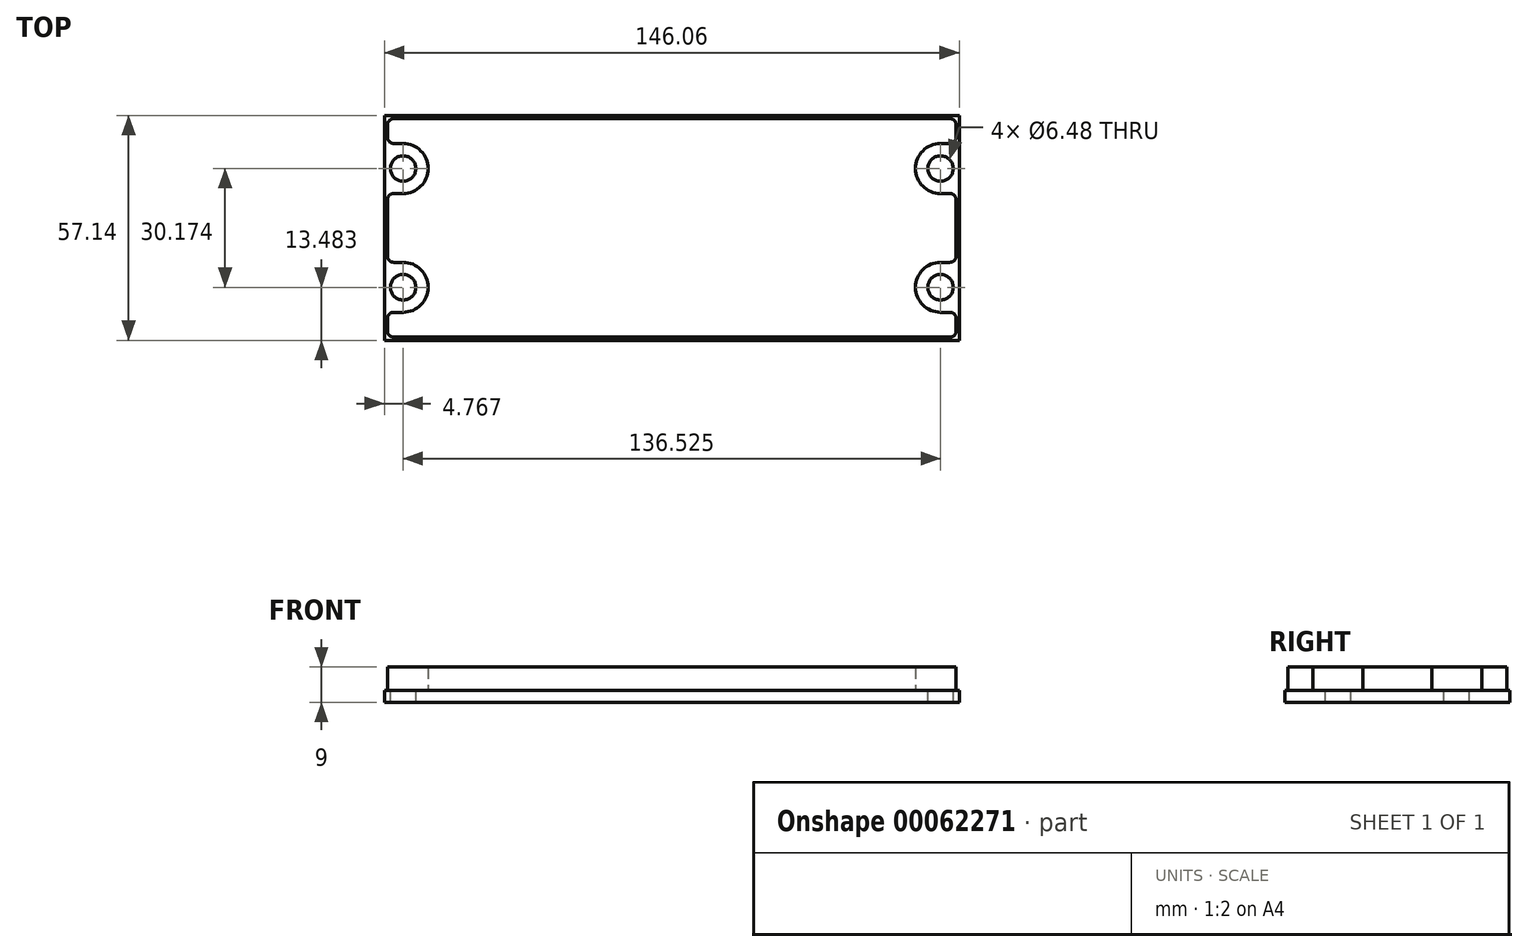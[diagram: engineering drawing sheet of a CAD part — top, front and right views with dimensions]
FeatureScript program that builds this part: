
annotation { "Feature Type Name" : "Feature", "Feature Type Description" : "" }
export const myFeature = defineFeature(function(context is Context, id is Id, definition is map)
    precondition{}
    {
        {
            var Q0;
            Q0=qCreatedBy(makeId("Top.planeOp"),FACE);
            var sketch = newSketch(context, id + "F0", { "sketchPlane" : qUnion([Q0])});
            skLineSegment(sketch, "E0.bottom", {"start": v(73.02, 28.57) * mm, "end": v(-73.03, 28.57) * mm});
            skLineSegment(sketch, "E0.top", {"start": v(73.02, -28.57) * mm, "end": v(-73.03, -28.57) * mm});
            skLineSegment(sketch, "E0.left", {"start": v(73.02, 28.57) * mm, "end": v(73.02, -28.57) * mm});
            skLineSegment(sketch, "E0.right", {"start": v(-73.03, 28.57) * mm, "end": v(-73.03, -28.57) * mm});
            skPoint(sketch, "E0.middle", {"position": v(0, 0) * mm});
            skLineSegment(sketch, "E1.bottom", {"start": v(72.22, 27.78) * mm, "end": v(-72.22, 27.78) * mm});
            skLineSegment(sketch, "E1.top", {"start": v(72.22, -27.78) * mm, "end": v(-72.22, -27.78) * mm});
            skLineSegment(sketch, "E1.left", {"start": v(72.22, 27.78) * mm, "end": v(72.22, 21.44) * mm});
            skLineSegment(sketch, "E1.right", {"start": v(-72.22, 27.78) * mm, "end": v(-72.22, 21.44) * mm});
            skArc(sketch, "E2", {"start": v(-68.26, 8.74) * mm, "mid": v(-61.91, 15.09) * mm, "end": v(-68.26, 21.44) * mm});
            skLineSegment(sketch, "E3", {"start": v(-68.26, 21.44) * mm, "end": v(-72.22, 21.44) * mm});
            skLineSegment(sketch, "E4", {"start": v(-68.26, 8.74) * mm, "end": v(-72.22, 8.74) * mm});
            skLineSegment(sketch, "E5.trimOffspring", {"start": v(-72.22, 8.74) * mm, "end": v(-72.22, -8.74) * mm});
            skCircle(sketch, "E6", {"center": v(-68.26, 15.09) * mm, "radius": 3.24 * mm});
            skLineSegment(sketch, "E7.MirrorCS", {"start": v(-68.26, -21.44) * mm, "end": v(-72.22, -21.44) * mm});
            skArc(sketch, "E8.MirrorCS", {"start": v(-68.26, -8.74) * mm, "mid": v(-61.91, -15.09) * mm, "end": v(-68.26, -21.44) * mm});
            skCircle(sketch, "E9.MirrorC", {"center": v(-68.26, -15.09) * mm, "radius": 3.24 * mm});
            skLineSegment(sketch, "E10.MirrorCS", {"start": v(-68.26, -8.74) * mm, "end": v(-72.22, -8.74) * mm});
            skLineSegment(sketch, "E11.MirrorCS", {"start": v(68.26, 8.74) * mm, "end": v(72.22, 8.74) * mm});
            skLineSegment(sketch, "E12.MirrorCS", {"start": v(68.26, 21.44) * mm, "end": v(72.22, 21.44) * mm});
            skLineSegment(sketch, "E13.MirrorCS", {"start": v(68.26, -21.44) * mm, "end": v(72.22, -21.44) * mm});
            skLineSegment(sketch, "E14.MirrorCS", {"start": v(68.26, -8.74) * mm, "end": v(72.22, -8.74) * mm});
            skCircle(sketch, "E15.MirrorC", {"center": v(68.26, 15.09) * mm, "radius": 3.24 * mm});
            skCircle(sketch, "E16.MirrorC", {"center": v(68.26, -15.09) * mm, "radius": 3.24 * mm});
            skArc(sketch, "E17.MirrorCS", {"start": v(68.26, 8.74) * mm, "mid": v(61.91, 15.09) * mm, "end": v(68.26, 21.44) * mm});
            skArc(sketch, "E18.MirrorCS", {"start": v(68.26, -8.74) * mm, "mid": v(61.91, -15.09) * mm, "end": v(68.26, -21.44) * mm});
            skLineSegment(sketch, "E19.trimOffspring", {"start": v(-72.22, -21.44) * mm, "end": v(-72.22, -27.78) * mm});
            skLineSegment(sketch, "E20.trimOffspring", {"start": v(72.22, -21.44) * mm, "end": v(72.22, -27.78) * mm});
            skLineSegment(sketch, "E21.trimOffspring", {"start": v(72.22, 8.74) * mm, "end": v(72.22, -8.74) * mm});
            skSolve(sketch);
        }
        {
            var Q0;
            Q0=qSketchRegion(id+"F0",true);
            var Q1;
            Q1=makeQuery(id+"F0.imprint","IMPRINT",FACE,{"disambiguationData":[TD([[makeQuery(id+"F0.imprint","IMPRINT",EDGE,{"derivedFrom":sQuery(id+"F0.wireOp",EDGE,"E1.bottom")}),1.0]])]});
            extrude(context, id + "F1", {"entities" : qUnion([Q0, Q1]), "oppositeDirection" : true, "depth" : 3 * mm, "offsetDistance" : 25 * mm});
        }
        {
            var Q0;
            Q0=makeQuery(id+"F0.imprint","IMPRINT",FACE,{"disambiguationData":[TD([[makeQuery(id+"F0.imprint","IMPRINT",EDGE,{"derivedFrom":sQuery(id+"F0.wireOp",EDGE,"E1.bottom")}),1.0]])]});
            extrude(context, id + "F2", {"entities" : qUnion([Q0]), "depth" : 6 * mm, "offsetDistance" : 25 * mm});
        }
        {
            var Q0;
            Q0=makeQuery(id+"F2.opExtrude","SWEPT_EDGE",EDGE,{"disambiguationData":[OSD([sQuery(id+"F0.wireOp",EDGE,"E1.bottom"),sQuery(id+"F0.wireOp",EDGE,"E1.right")])]});
            var Q1;
            Q1=makeQuery(id+"F2.opExtrude","SWEPT_EDGE",EDGE,{"disambiguationData":[OSD([sQuery(id+"F0.wireOp",EDGE,"E1.right"),sQuery(id+"F0.wireOp",EDGE,"E3")])]});
            var Q2;
            Q2=makeQuery(id+"F2.opExtrude","SWEPT_EDGE",EDGE,{"disambiguationData":[OSD([sQuery(id+"F0.wireOp",EDGE,"E4"),sQuery(id+"F0.wireOp",EDGE,"E5.trimOffspring")])]});
            var Q3;
            Q3=makeQuery(id+"F2.opExtrude","SWEPT_EDGE",EDGE,{"disambiguationData":[OSD([sQuery(id+"F0.wireOp",EDGE,"E5.trimOffspring"),sQuery(id+"F0.wireOp",EDGE,"E10.MirrorCS")])]});
            var Q4;
            Q4=makeQuery(id+"F2.opExtrude","SWEPT_EDGE",EDGE,{"disambiguationData":[OSD([sQuery(id+"F0.wireOp",EDGE,"E7.MirrorCS"),sQuery(id+"F0.wireOp",EDGE,"E19.trimOffspring")])]});
            var Q5;
            Q5=makeQuery(id+"F2.opExtrude","SWEPT_EDGE",EDGE,{"disambiguationData":[OSD([sQuery(id+"F0.wireOp",EDGE,"E1.top"),sQuery(id+"F0.wireOp",EDGE,"E19.trimOffspring")])]});
            var Q6;
            Q6=makeQuery(id+"F2.opExtrude","SWEPT_EDGE",EDGE,{"disambiguationData":[OSD([sQuery(id+"F0.wireOp",EDGE,"E1.left"),sQuery(id+"F0.wireOp",EDGE,"E12.MirrorCS")])]});
            var Q7;
            Q7=makeQuery(id+"F2.opExtrude","SWEPT_EDGE",EDGE,{"disambiguationData":[OSD([sQuery(id+"F0.wireOp",EDGE,"E14.MirrorCS"),sQuery(id+"F0.wireOp",EDGE,"E21.trimOffspring")])]});
            var Q8;
            Q8=makeQuery(id+"F2.opExtrude","SWEPT_EDGE",EDGE,{"disambiguationData":[OSD([sQuery(id+"F0.wireOp",EDGE,"E1.top"),sQuery(id+"F0.wireOp",EDGE,"E20.trimOffspring")])]});
            var Q9;
            Q9=makeQuery(id+"F2.opExtrude","SWEPT_EDGE",EDGE,{"disambiguationData":[OSD([sQuery(id+"F0.wireOp",EDGE,"E13.MirrorCS"),sQuery(id+"F0.wireOp",EDGE,"E20.trimOffspring")])]});
            var Q10;
            Q10=makeQuery(id+"F2.opExtrude","SWEPT_EDGE",EDGE,{"disambiguationData":[OSD([sQuery(id+"F0.wireOp",EDGE,"E11.MirrorCS"),sQuery(id+"F0.wireOp",EDGE,"E21.trimOffspring")])]});
            var Q11;
            Q11=makeQuery(id+"F2.opExtrude","SWEPT_EDGE",EDGE,{"disambiguationData":[OSD([sQuery(id+"F0.wireOp",EDGE,"E1.bottom"),sQuery(id+"F0.wireOp",EDGE,"E1.left")])]});
            fillet(context, id + "F3", {"entities" : qUnion([Q0, Q1, Q2, Q3, Q4, Q5, Q6, Q7, Q8, Q9, Q10, Q11]), "radius" : 1.59 * mm, "tangentPropagation" : true, "allowEdgeOverflow" : false});
        }
    });
